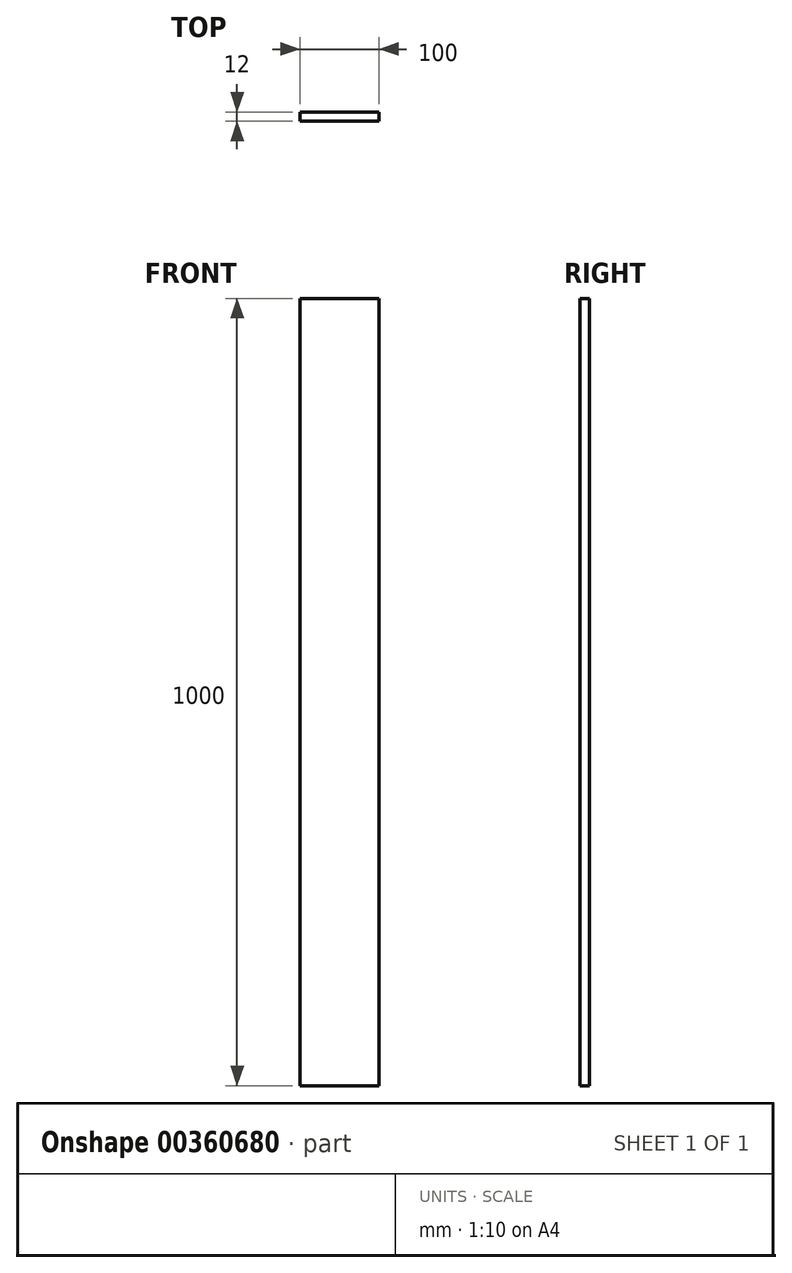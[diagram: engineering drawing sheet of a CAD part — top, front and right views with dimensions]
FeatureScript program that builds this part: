
annotation { "Feature Type Name" : "Feature", "Feature Type Description" : "" }
export const myFeature = defineFeature(function(context is Context, id is Id, definition is map)
    precondition{}
    {
        {
            var Q0;
            Q0=qCreatedBy(makeId("Front.planeOp"),FACE);
            var sketch = newSketch(context, id + "F0", { "sketchPlane" : qUnion([Q0])});
            skLineSegment(sketch, "E0.bottom", {"start": v(0, 0) * mm, "end": v(100, 0) * mm});
            skLineSegment(sketch, "E0.top", {"start": v(0, 1000) * mm, "end": v(100, 1000) * mm});
            skLineSegment(sketch, "E0.left", {"start": v(0, 0) * mm, "end": v(0, 1000) * mm});
            skLineSegment(sketch, "E0.right", {"start": v(100, 0) * mm, "end": v(100, 1000) * mm});
            skSolve(sketch);
        }
        {
            var Q0;
            Q0=makeQuery(id+"F0.imprint","IMPRINT",FACE,{"disambiguationData":[TD([[makeQuery(id+"F0.imprint","IMPRINT",EDGE,{"derivedFrom":sQuery(id+"F0.wireOp",EDGE,"E0.bottom")}),1.0]])]});
            extrude(context, id + "F1", {"entities" : qUnion([Q0]), "depth" : 12 * mm});
        }
    });
